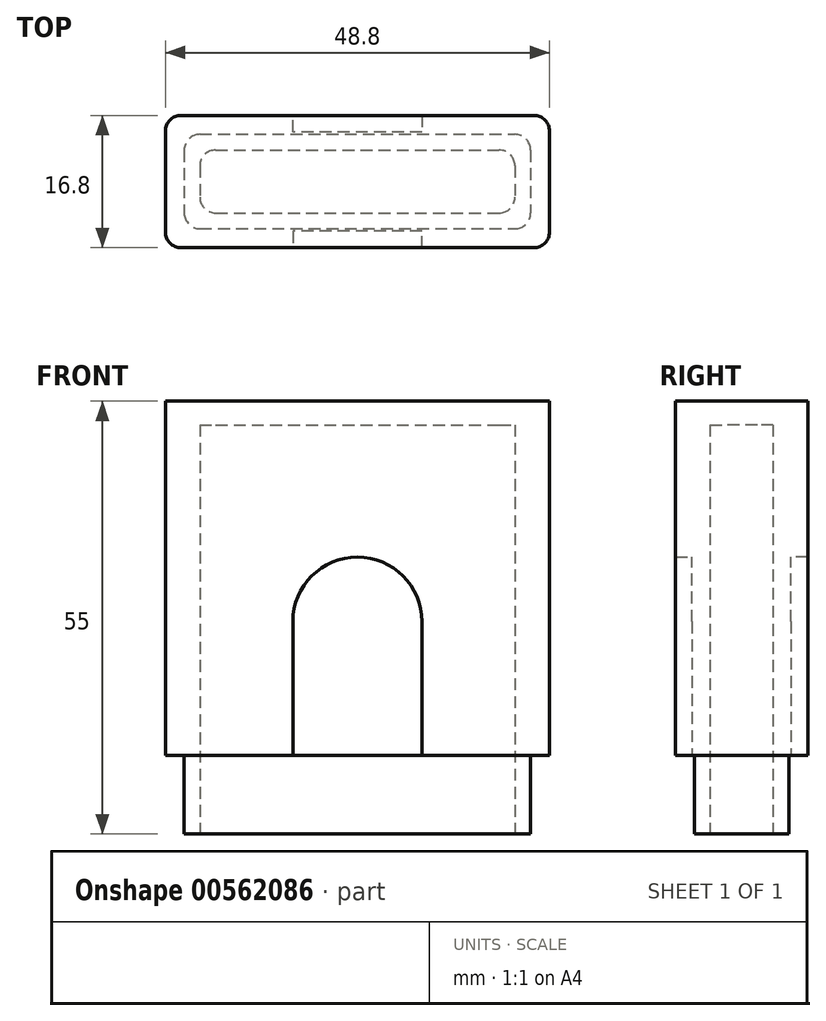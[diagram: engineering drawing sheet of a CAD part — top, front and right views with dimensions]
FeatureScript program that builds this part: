
annotation { "Feature Type Name" : "Feature", "Feature Type Description" : "" }
export const myFeature = defineFeature(function(context is Context, id is Id, definition is map)
    precondition{}
    {
        {
            var Q0;
            Q0=qCreatedBy(makeId("Top.planeOp"),FACE);
            var sketch = newSketch(context, id + "F0", { "sketchPlane" : qUnion([Q0])});
            skLineSegment(sketch, "E0.bottom", {"start": v(-23.3, 5.1) * mm, "end": v(16.7, 5.1) * mm});
            skLineSegment(sketch, "E0.top", {"start": v(-23.3, -2.9) * mm, "end": v(16.7, -2.9) * mm});
            skLineSegment(sketch, "E0.left", {"start": v(-23.3, 5.1) * mm, "end": v(-23.3, -2.9) * mm});
            skLineSegment(sketch, "E0.right", {"start": v(16.7, 5.1) * mm, "end": v(16.7, -2.9) * mm});
            skLineSegment(sketch, "E1.0", {"start": v(-25.3, 7.1) * mm, "end": v(-25.3, -4.9) * mm});
            skLineSegment(sketch, "E1.1", {"start": v(-25.3, 7.1) * mm, "end": v(18.7, 7.1) * mm});
            skLineSegment(sketch, "E1.2", {"start": v(18.7, 7.1) * mm, "end": v(18.7, -4.9) * mm});
            skLineSegment(sketch, "E1.3", {"start": v(-25.3, -4.9) * mm, "end": v(18.7, -4.9) * mm});
            skLineSegment(sketch, "E2.0", {"start": v(-25.7, 7.5) * mm, "end": v(-25.7, -5.3) * mm});
            skLineSegment(sketch, "E2.1", {"start": v(-25.7, 7.5) * mm, "end": v(19.1, 7.5) * mm});
            skLineSegment(sketch, "E2.2", {"start": v(19.1, 7.5) * mm, "end": v(19.1, -5.3) * mm});
            skLineSegment(sketch, "E2.3", {"start": v(-25.7, -5.3) * mm, "end": v(19.1, -5.3) * mm});
            skLineSegment(sketch, "E3.0", {"start": v(-27.7, 9.5) * mm, "end": v(-27.7, -7.3) * mm});
            skLineSegment(sketch, "E3.1", {"start": v(-27.7, 9.5) * mm, "end": v(21.1, 9.5) * mm});
            skLineSegment(sketch, "E3.2", {"start": v(21.1, 9.5) * mm, "end": v(21.1, -7.3) * mm});
            skLineSegment(sketch, "E3.3", {"start": v(-27.7, -7.3) * mm, "end": v(21.1, -7.3) * mm});
            skSolve(sketch);
        }
        {
            var Q0;
            Q0=makeQuery(id+"F0.imprint","IMPRINT",FACE,{"disambiguationData":[TD([[makeQuery(id+"F0.imprint","IMPRINT",EDGE,{"derivedFrom":sQuery(id+"F0.wireOp",EDGE,"E0.bottom")}),-1.0]])]});
            var Q1;
            Q1=makeQuery(id+"F0.imprint","IMPRINT",FACE,{"disambiguationData":[TD([[makeQuery(id+"F0.imprint","IMPRINT",EDGE,{"derivedFrom":sQuery(id+"F0.wireOp",EDGE,"E0.bottom")}),1.0]])]});
            var Q2;
            Q2=makeQuery(id+"F0.imprint","IMPRINT",FACE,{"disambiguationData":[TD([[makeQuery(id+"F0.imprint","IMPRINT",EDGE,{"derivedFrom":sQuery(id+"F0.wireOp",EDGE,"E1.0")}),-1.0]])]});
            var Q3;
            Q3=makeQuery(id+"F0.imprint","IMPRINT",FACE,{"disambiguationData":[TD([[makeQuery(id+"F0.imprint","IMPRINT",EDGE,{"derivedFrom":sQuery(id+"F0.wireOp",EDGE,"E2.0")}),-1.0]])]});
            extrude(context, id + "F1", {"entities" : qUnion([Q0, Q1, Q2, Q3]), "depth" : 45 * mm, "offsetDistance" : 25 * mm});
        }
        {
            var Q0;
            Q0=makeQuery(id+"F0.imprint","IMPRINT",FACE,{"disambiguationData":[TD([[makeQuery(id+"F0.imprint","IMPRINT",EDGE,{"derivedFrom":sQuery(id+"F0.wireOp",EDGE,"E0.bottom")}),-1.0]])]});
            extrude(context, id + "F2", {"entities" : qUnion([Q0]), "operationType" : NewBodyOperationType.REMOVE, "depth" : 42 * mm, "offsetDistance" : 25 * mm});
        }
        {
            var Q0;
            Q0=makeQuery(id+"F0.imprint","IMPRINT",FACE,{"disambiguationData":[TD([[makeQuery(id+"F0.imprint","IMPRINT",EDGE,{"derivedFrom":sQuery(id+"F0.wireOp",EDGE,"E0.bottom")}),1.0]])]});
            extrude(context, id + "F3", {"entities" : qUnion([Q0]), "operationType" : NewBodyOperationType.ADD, "oppositeDirection" : true, "depth" : 10 * mm, "offsetDistance" : 25 * mm});
        }
        {
            var Q0;
            Q0=makeQuery(id+"F1.opExtrude","SWEPT_EDGE",EDGE,{"disambiguationData":[OSD([sQuery(id+"F0.wireOp",EDGE,"E3.0"),sQuery(id+"F0.wireOp",EDGE,"E3.3")])]});
            var Q1;
            Q1=makeQuery(id+"F1.opExtrude","SWEPT_EDGE",EDGE,{"disambiguationData":[OSD([sQuery(id+"F0.wireOp",EDGE,"E3.0"),sQuery(id+"F0.wireOp",EDGE,"E3.1")])]});
            var Q2;
            Q2=makeQuery(id+"F1.opExtrude","SWEPT_EDGE",EDGE,{"disambiguationData":[OSD([sQuery(id+"F0.wireOp",EDGE,"E3.2"),sQuery(id+"F0.wireOp",EDGE,"E3.3")])]});
            var Q3;
            Q3=makeQuery(id+"F1.opExtrude","SWEPT_EDGE",EDGE,{"disambiguationData":[OSD([sQuery(id+"F0.wireOp",EDGE,"E3.1"),sQuery(id+"F0.wireOp",EDGE,"E3.2")])]});
            fillet(context, id + "F4", {"entities" : qUnion([Q0, Q1, Q2, Q3]), "radius" : 2 * mm, "tangentPropagation" : true, "allowEdgeOverflow" : false});
        }
        {
            var Q0;
            {var subQ0=sQuery(id+"F0.wireOp",EDGE,"E0.left");var subQ1=sQuery(id+"F0.wireOp",EDGE,"E0.bottom");Q0=makeQuery(id+"F3.boolean.opBoolean","MERGE",EDGE,{"derivedFrom":[makeQuery(id+"F2.boolean.opBoolean","COPY",EDGE,{"derivedFrom":makeQuery(id+"F2.opExtrude","SWEPT_EDGE",EDGE,{"disambiguationData":[OSD([subQ1,subQ0])]})}),makeQuery(id+"F3.opExtrude","SWEPT_EDGE",EDGE,{"disambiguationData":[OSD([subQ1,subQ0])]})]});}
            var Q1;
            {var subQ0=sQuery(id+"F0.wireOp",EDGE,"E0.left");var subQ1=sQuery(id+"F0.wireOp",EDGE,"E0.top");Q1=makeQuery(id+"F3.boolean.opBoolean","MERGE",EDGE,{"derivedFrom":[makeQuery(id+"F2.boolean.opBoolean","COPY",EDGE,{"derivedFrom":makeQuery(id+"F2.opExtrude","SWEPT_EDGE",EDGE,{"disambiguationData":[OSD([subQ1,subQ0])]})}),makeQuery(id+"F3.opExtrude","SWEPT_EDGE",EDGE,{"disambiguationData":[OSD([subQ1,subQ0])]})]});}
            var Q2;
            {var subQ0=sQuery(id+"F0.wireOp",EDGE,"E0.right");var subQ1=sQuery(id+"F0.wireOp",EDGE,"E0.bottom");Q2=makeQuery(id+"F3.boolean.opBoolean","MERGE",EDGE,{"derivedFrom":[makeQuery(id+"F2.boolean.opBoolean","COPY",EDGE,{"derivedFrom":makeQuery(id+"F2.opExtrude","SWEPT_EDGE",EDGE,{"disambiguationData":[OSD([subQ1,subQ0])]})}),makeQuery(id+"F3.opExtrude","SWEPT_EDGE",EDGE,{"disambiguationData":[OSD([subQ1,subQ0])]})]});}
            var Q3;
            {var subQ0=sQuery(id+"F0.wireOp",EDGE,"E0.right");var subQ1=sQuery(id+"F0.wireOp",EDGE,"E0.top");Q3=makeQuery(id+"F3.boolean.opBoolean","MERGE",EDGE,{"derivedFrom":[makeQuery(id+"F2.boolean.opBoolean","COPY",EDGE,{"derivedFrom":makeQuery(id+"F2.opExtrude","SWEPT_EDGE",EDGE,{"disambiguationData":[OSD([subQ1,subQ0])]})}),makeQuery(id+"F3.opExtrude","SWEPT_EDGE",EDGE,{"disambiguationData":[OSD([subQ1,subQ0])]})]});}
            fillet(context, id + "F5", {"entities" : qUnion([Q0, Q1, Q2, Q3]), "radius" : 2 * mm, "tangentPropagation" : true, "allowEdgeOverflow" : false});
        }
        {
            var Q0;
            Q0=makeQuery(id+"F3.opExtrude","SWEPT_EDGE",EDGE,{"disambiguationData":[OSD([sQuery(id+"F0.wireOp",EDGE,"E1.2"),sQuery(id+"F0.wireOp",EDGE,"E1.3")])]});
            var Q1;
            Q1=makeQuery(id+"F3.opExtrude","SWEPT_EDGE",EDGE,{"disambiguationData":[OSD([sQuery(id+"F0.wireOp",EDGE,"E1.1"),sQuery(id+"F0.wireOp",EDGE,"E1.2")])]});
            var Q2;
            Q2=makeQuery(id+"F3.opExtrude","SWEPT_EDGE",EDGE,{"disambiguationData":[OSD([sQuery(id+"F0.wireOp",EDGE,"E1.0"),sQuery(id+"F0.wireOp",EDGE,"E1.3")])]});
            var Q3;
            Q3=makeQuery(id+"F3.opExtrude","SWEPT_EDGE",EDGE,{"disambiguationData":[OSD([sQuery(id+"F0.wireOp",EDGE,"E1.0"),sQuery(id+"F0.wireOp",EDGE,"E1.1")])]});
            fillet(context, id + "F6", {"entities" : qUnion([Q0, Q1, Q2, Q3]), "radius" : 2 * mm, "tangentPropagation" : true, "allowEdgeOverflow" : false});
        }
        {
            var Q0;
            Q0=makeQuery(id+"F1.opExtrude","CAP_FACE",FACE,{"disambiguationData":[OSD([sQuery(id+"F0.wireOp",EDGE,"E3.0"),sQuery(id+"F0.wireOp",EDGE,"E3.1"),sQuery(id+"F0.wireOp",EDGE,"E3.2"),sQuery(id+"F0.wireOp",EDGE,"E3.3")])],"isStart":true});
            var sketch = newSketch(context, id + "F7", { "sketchPlane" : qUnion([Q0])});
            skLineSegment(sketch, "E4", {"start": v(-3.3, 7.3) * mm, "end": v(4.9, 7.3) * mm});
            skLineSegment(sketch, "E5", {"start": v(4.9, 7.3) * mm, "end": v(4.9, 5.2) * mm});
            skLineSegment(sketch, "E6", {"start": v(4.9, 5.2) * mm, "end": v(-11.5, 5.2) * mm});
            skLineSegment(sketch, "E7", {"start": v(-11.5, 5.2) * mm, "end": v(-11.5, 7.3) * mm});
            skLineSegment(sketch, "E8", {"start": v(-11.5, 7.3) * mm, "end": v(-3.3, 7.3) * mm});
            skLineSegment(sketch, "E9", {"start": v(-3.3, -9.5) * mm, "end": v(4.9, -9.5) * mm});
            skLineSegment(sketch, "E10", {"start": v(4.9, -9.5) * mm, "end": v(4.9, -7.4) * mm});
            skLineSegment(sketch, "E11", {"start": v(4.9, -7.4) * mm, "end": v(-11.5, -7.4) * mm});
            skLineSegment(sketch, "E12", {"start": v(-11.5, -7.4) * mm, "end": v(-11.5, -9.5) * mm});
            skSolve(sketch);
        }
        {
            var Q0;
            Q0=makeQuery(id+"F7.imprint","IMPRINT",FACE,{"disambiguationData":[TD([[makeQuery(id+"F7.imprint","IMPRINT",EDGE,{"derivedFrom":sQuery(id+"F7.wireOp",EDGE,"E4")}),-1.0]])]});
            var Q1;
            {var subQ1=sQuery(id+"F7.wireOp",EDGE,"E9");Q1=makeQuery(id+"F7.imprint","IMPRINT",FACE,{"disambiguationData":[TD([[makeQuery(id+"F7.imprint","IMPRINT",EDGE,{"derivedFrom":subQ1}),1.0]])]});}
            extrude(context, id + "F8", {"entities" : qUnion([Q0, Q1]), "operationType" : NewBodyOperationType.REMOVE, "oppositeDirection" : true, "depth" : 25.2 * mm, "offsetDistance" : 25 * mm});
        }
        {
            var Q0;
            Q0=makeQuery(id+"F8.boolean.opBoolean","COPY",EDGE,{"derivedFrom":makeQuery(id+"F8.opExtrude","CAP_EDGE",EDGE,{"disambiguationData":[OSD([sQuery(id+"F7.wireOp",EDGE,"E7")])],"isStart":false})});
            var Q1;
            Q1=makeQuery(id+"F8.boolean.opBoolean","COPY",EDGE,{"derivedFrom":makeQuery(id+"F8.opExtrude","CAP_EDGE",EDGE,{"disambiguationData":[OSD([sQuery(id+"F7.wireOp",EDGE,"E5")])],"isStart":false})});
            var Q2;
            Q2=makeQuery(id+"F8.boolean.opBoolean","COPY",EDGE,{"derivedFrom":makeQuery(id+"F8.opExtrude","CAP_EDGE",EDGE,{"disambiguationData":[OSD([sQuery(id+"F7.wireOp",EDGE,"E10")])],"isStart":false})});
            var Q3;
            Q3=makeQuery(id+"F8.boolean.opBoolean","COPY",EDGE,{"derivedFrom":makeQuery(id+"F8.opExtrude","CAP_EDGE",EDGE,{"disambiguationData":[OSD([sQuery(id+"F7.wireOp",EDGE,"E12")])],"isStart":false})});
            fillet(context, id + "F9", {"entities" : qUnion([Q0, Q1, Q2, Q3]), "radius" : 8.2 * mm, "tangentPropagation" : true, "allowEdgeOverflow" : false});
        }
    });
